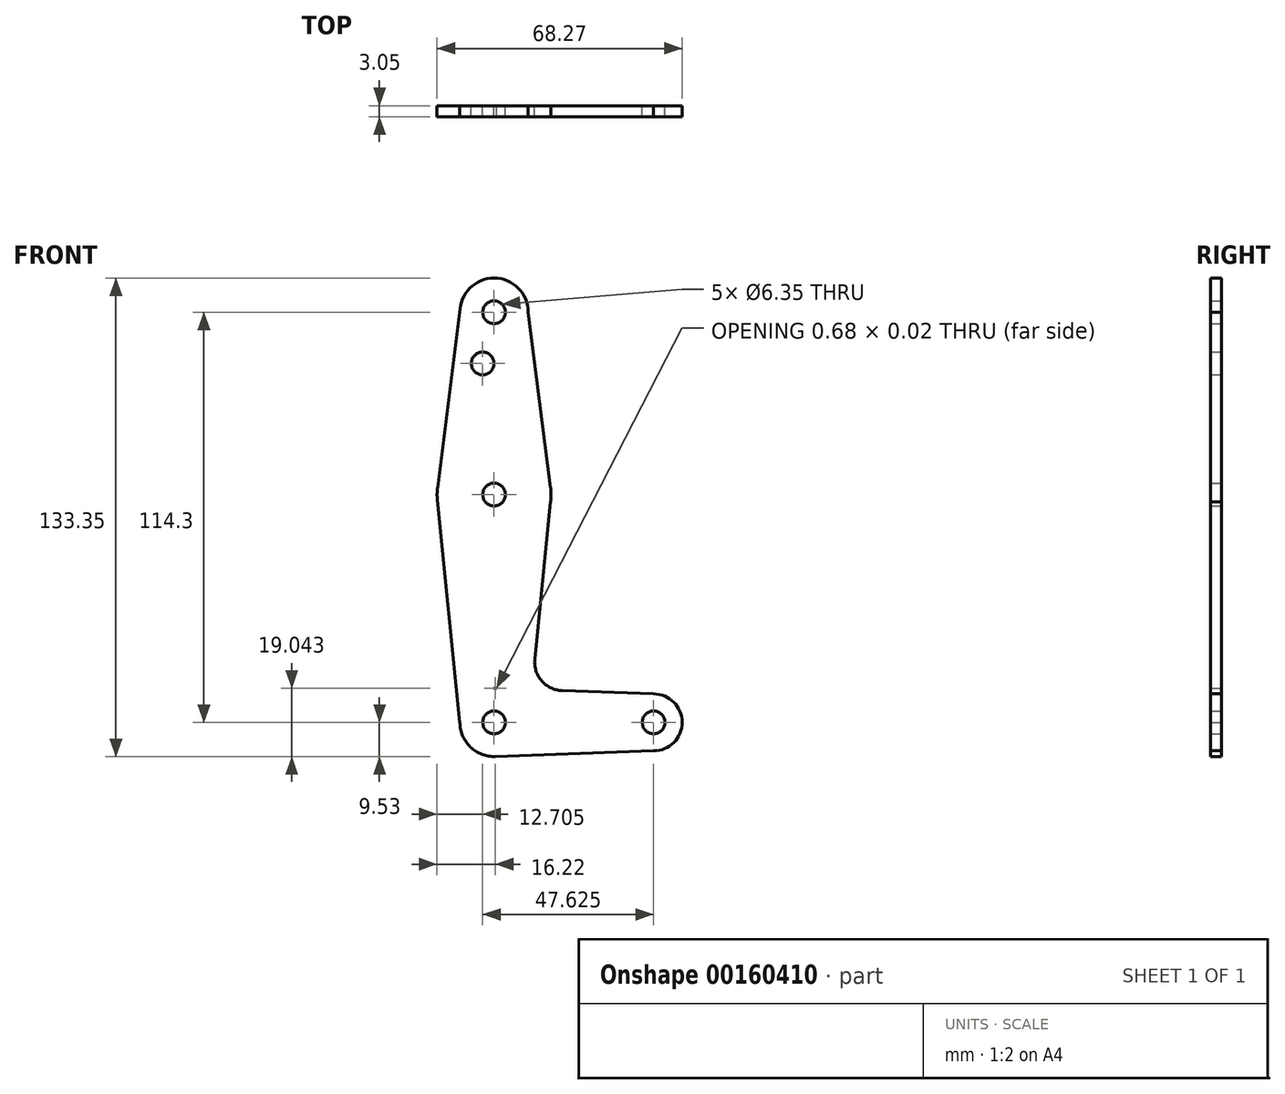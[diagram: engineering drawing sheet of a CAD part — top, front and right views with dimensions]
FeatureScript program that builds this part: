
annotation { "Feature Type Name" : "Feature", "Feature Type Description" : "" }
export const myFeature = defineFeature(function(context is Context, id is Id, definition is map)
    precondition{}
    {
        {
            var Q0;
            Q0=qCreatedBy(makeId("Front.planeOp"),FACE);
            var sketch = newSketch(context, id + "F0", { "sketchPlane" : qUnion([Q0])});
            skCircle(sketch, "E0", {"center": v(0, 0) * mm, "radius": 15.87 * mm});
            skCircle(sketch, "E1", {"center": v(0, 50.8) * mm, "radius": 9.53 * mm});
            skCircle(sketch, "E2", {"center": v(0, -63.5) * mm, "radius": 9.53 * mm});
            skLineSegment(sketch, "E3", {"start": v(0, 36.53) * mm, "end": v(-3.17, 36.53) * mm});
            skCircle(sketch, "E4", {"center": v(-3.17, 36.53) * mm, "radius": 3.18 * mm});
            skCircle(sketch, "E5", {"center": v(0, 50.8) * mm, "radius": 3.18 * mm});
            skCircle(sketch, "E6", {"center": v(0, 0) * mm, "radius": 3.18 * mm});
            skCircle(sketch, "E7", {"center": v(0, -63.5) * mm, "radius": 3.18 * mm});
            skCircle(sketch, "E8", {"center": v(44.45, -63.5) * mm, "radius": 7.94 * mm});
            skCircle(sketch, "E9", {"center": v(44.45, -63.5) * mm, "radius": 3.18 * mm});
            skLineSegment(sketch, "E10", {"start": v(-9.52, 50.8) * mm, "end": v(-15.75, 2) * mm});
            skLineSegment(sketch, "E11", {"start": v(9.53, 50.8) * mm, "end": v(15.75, 2) * mm});
            skLineSegment(sketch, "E12", {"start": v(-15.8, -1.6) * mm, "end": v(-9.52, -63.5) * mm});
            skLineSegment(sketch, "E13", {"start": v(15.75, -2) * mm, "end": v(11.34, -45.91) * mm});
            skLineSegment(sketch, "E14", {"start": v(44.45, -71.44) * mm, "end": v(0, -73.03) * mm});
            skLineSegment(sketch, "E15", {"start": v(44.45, -55.56) * mm, "end": v(18.97, -54.65) * mm});
            skLineSegment(sketch, "E16.trimOffspring", {"start": v(0.68, -54) * mm, "end": v(0, -53.98) * mm});
            skPoint(sketch, "E17.visualSharp", {"position": v(10.5, -54.35) * mm});
            skArc(sketch, "E17.filletArc", {"start": v(11.34, -45.91) * mm, "mid": v(13.26, -51.93) * mm, "end": v(18.97, -54.65) * mm});
            skSolve(sketch);
        }
        {
            var Q0;
            Q0=makeQuery(id+"F0.imprint","IMPRINT",FACE,{"disambiguationData":[TD([[makeQuery(id+"F0.imprint","IMPRINT",EDGE,{"derivedFrom":sQuery(id+"F0.wireOp",EDGE,"E5")}),-1.0]])]});
            var Q1;
            Q1=makeQuery(id+"F0.imprint","IMPRINT",FACE,{"disambiguationData":[TD([[makeQuery(id+"F0.imprint","IMPRINT",EDGE,{"derivedFrom":sQuery(id+"F0.wireOp",EDGE,"E4")}),-1.0]])]});
            var Q2;
            Q2=makeQuery(id+"F0.imprint","IMPRINT",FACE,{"disambiguationData":[TD([[makeQuery(id+"F0.imprint","IMPRINT",EDGE,{"derivedFrom":sQuery(id+"F0.wireOp",EDGE,"E6")}),-1.0]])]});
            var Q3;
            {var subQ5=sQuery(id+"F0.wireOp",EDGE,"E12");Q3=makeQuery(id+"F0.imprint","IMPRINT",FACE,{"disambiguationData":[TD([[makeQuery(id+"F0.imprint","IMPRINT",EDGE,{"derivedFrom":subQ5}),1.0]])]});}
            var Q4;
            Q4=makeQuery(id+"F0.imprint","IMPRINT",FACE,{"disambiguationData":[TD([[makeQuery(id+"F0.imprint","IMPRINT",EDGE,{"derivedFrom":sQuery(id+"F0.wireOp",EDGE,"E9")}),-1.0]])]});
            var Q5;
            Q5=makeQuery(id+"F0.imprint","IMPRINT",FACE,{"disambiguationData":[TD([[makeQuery(id+"F0.imprint","IMPRINT",EDGE,{"derivedFrom":sQuery(id+"F0.wireOp",EDGE,"E7")}),-1.0]])]});
            extrude(context, id + "F1", {"entities" : qUnion([Q0, Q1, Q2, Q3, Q4, Q5]), "depth" : 3.05 * mm});
        }
    });
